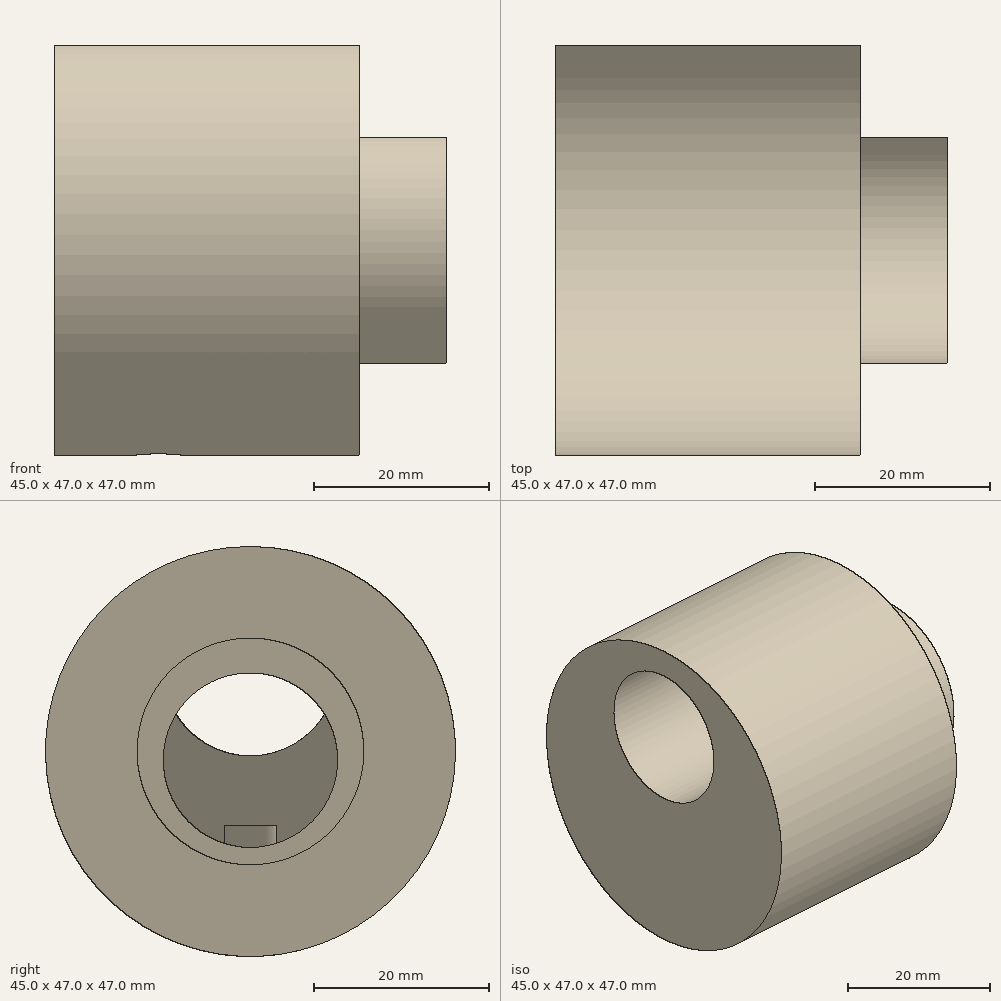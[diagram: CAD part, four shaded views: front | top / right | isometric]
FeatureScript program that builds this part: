
annotation { "Feature Type Name" : "Feature", "Feature Type Description" : "" }
export const myFeature = defineFeature(function(context is Context, id is Id, definition is map)
    precondition{}
    {
        {
            var Q0;
            Q0=qCreatedBy(makeId("Front.planeOp"),FACE);
            var sketch = newSketch(context, id + "F0", { "sketchPlane" : qUnion([Q0])});
            skLineSegment(sketch, "E0", {"start": v(-35, 0) * mm, "end": v(-35, 23.5) * mm});
            skLineSegment(sketch, "E1", {"start": v(-35, 23.5) * mm, "end": v(0, 23.5) * mm});
            skLineSegment(sketch, "E2", {"start": v(0, 23.5) * mm, "end": v(0, 13) * mm});
            skLineSegment(sketch, "E3", {"start": v(0, 13) * mm, "end": v(10, 13) * mm});
            skLineSegment(sketch, "E4", {"start": v(10, 13) * mm, "end": v(10, 0) * mm});
            skLineSegment(sketch, "E5", {"start": v(10, 0) * mm, "end": v(-35, 0) * mm});
            skLineSegment(sketch, "E6", {"start": v(-48.91, 0) * mm, "end": v(42.52, 0) * mm, "construction": true});
            skSolve(sketch);
        }
        {
            var Q0;
            Q0 = qSketchRegion(id + "F0", true);
            var Q1;
            Q1=sQuery(id+"F0.wireOp",EDGE,"E6");
            revolve(context, id + "F1", {"entities" : qUnion([Q0]), "axis" : qUnion([Q1]), "revolveType" : RevolveType.FULL});
        }
        {
            var Q0;
            Q0=makeQuery(id+"F1.opRevolve","SWEPT_FACE",FACE,{"disambiguationData":[OSD([sQuery(id+"F0.wireOp",EDGE,"E4")])]});
            var sketch = newSketch(context, id + "F2", { "sketchPlane" : qUnion([Q0])});
            skCircle(sketch, "E7", {"center": v(0, -1) * mm, "radius": 10 * mm});
            skSolve(sketch);
        }
        {
            var Q0;
            Q0 = qSketchRegion(id + "F2", true);
            extrude(context, id + "F3", {"entities" : qUnion([Q0]), "operationType" : NewBodyOperationType.REMOVE, "oppositeDirection" : true, "depth" : 25 * mm});
        }
        {
            var Q0;
            Q0=makeQuery(id+"F1.opRevolve","SWEPT_FACE",FACE,{"disambiguationData":[OSD([sQuery(id+"F0.wireOp",EDGE,"E0")])]});
            var sketch = newSketch(context, id + "F4", { "sketchPlane" : qUnion([Q0])});
            skCircle(sketch, "E8", {"center": v(0, 9.5) * mm, "radius": 10 * mm});
            skSolve(sketch);
        }
        {
            var Q0;
            Q0 = qSketchRegion(id + "F4", true);
            extrude(context, id + "F5", {"entities" : qUnion([Q0]), "operationType" : NewBodyOperationType.REMOVE, "oppositeDirection" : true, "depth" : 20 * mm});
        }
        {
            var Q0;
            Q0=makeQuery(id+"F3.boolean.opBoolean","COPY",FACE,{"derivedFrom":makeQuery(id+"F3.opExtrude","CAP_FACE",FACE,{"disambiguationData":[OSD([sQuery(id+"F2.wireOp",EDGE,"E7")])],"isStart":false})});
            var sketch = newSketch(context, id + "F6", { "sketchPlane" : qUnion([Q0])});
            skCircle(sketch, "E9", {"center": v(0, 4.25) * mm, "radius": 15.25 * mm});
            skPoint(sketch, "E9.first.point", {"position": v(0, -11) * mm});
            skPoint(sketch, "E9.second.point", {"position": v(0, 19.5) * mm});
            skPoint(sketch, "E9.second.point.positionSnap0", {"position": v(0, -0.5) * mm});
            skPoint(sketch, "E9.third.point", {"position": v(14.5, -0.5) * mm});
            skPoint(sketch, "E9.third.point.positionSnap0", {"position": v(0, -0.5) * mm});
            skSolve(sketch);
        }
        {
            var Q0;
            Q0 = qSketchRegion(id + "F6", true);
            extrude(context, id + "F7", {"entities" : qUnion([Q0]), "operationType" : NewBodyOperationType.REMOVE, "depth" : 5 * mm});
        }
        {
            var Q0;
            Q0=qCreatedBy(makeId("Top.planeOp"),FACE);
            cPlane(context, id + "F8", {"entities" : qUnion([Q0]), "cplaneType" : CPlaneType.OFFSET, "offset" : (47 / 2) * mm, "oppositeDirection" : true, "width" : 150 * mm, "height" : 150 * mm});
        }
        {
            var Q0;
            Q0=qCreatedBy(id+"F8.planeOp",FACE);
            var sketch = newSketch(context, id + "F9", { "sketchPlane" : qUnion([Q0])});
            skCircle(sketch, "E10", {"center": v(-23, 0) * mm, "radius": 3 * mm});
            skSolve(sketch);
        }
        {
            var Q0;
            Q0 = qSketchRegion(id + "F9", true);
            extrude(context, id + "F10", {"entities" : qUnion([Q0]), "operationType" : NewBodyOperationType.REMOVE, "depth" : 15 * mm});
        }
    });
